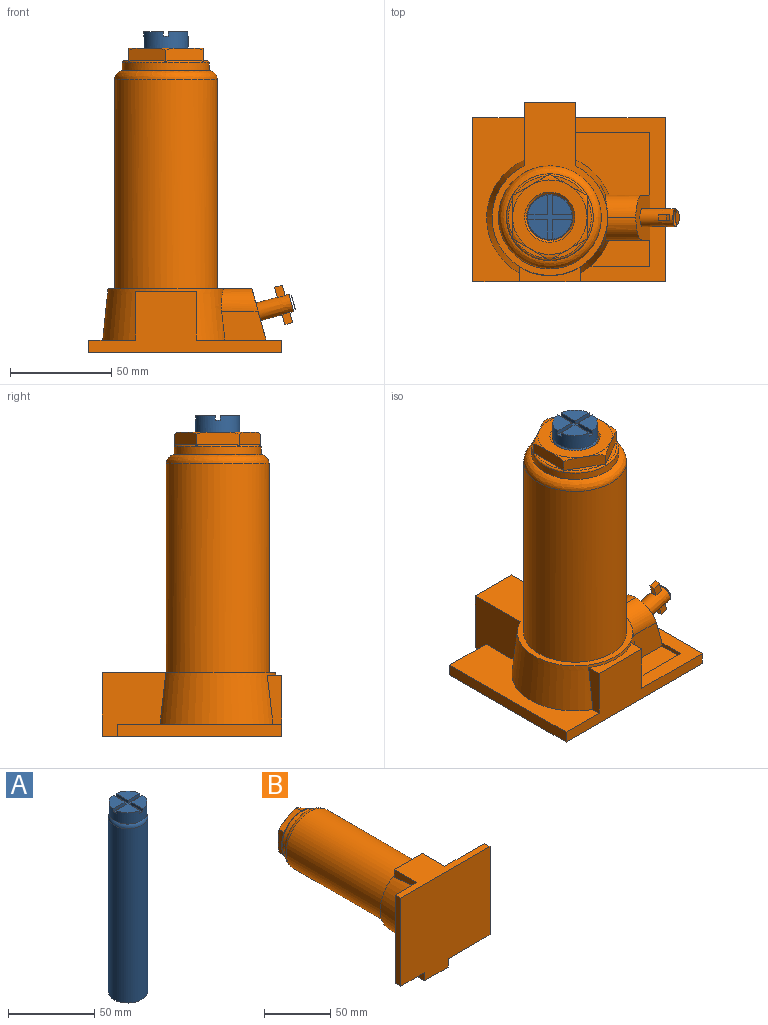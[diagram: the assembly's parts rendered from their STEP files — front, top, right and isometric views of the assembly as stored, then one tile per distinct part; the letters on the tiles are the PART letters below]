
ASSEMBLY  parts=2 mates=1
PART A: 18 faces, bbox 24.7x24.7x135 mm
  f0: plane 9.76x9.76mm, normal (0,0,1), area 70.6mm2, adj f2,f8,f16
  f1: plane 9.76x9.76mm, normal (0,0,1), area 70.6mm2, adj f3,f8,f15
  f2: plane 9.76x2.11mm, normal (0,1,0), area 20.6mm2, adj f0,f8,f11,f16
  f3: plane 9.76x2.11mm, normal (0,-1,0), area 20.6mm2, adj f1,f8,f11,f15
  f4: plane 9.76x9.76mm, normal (0,0,1), area 70.6mm2, adj f8,f12,f17
  f5: cylinder r=11.43mm len=124mm, axis (0,0,-1), area 8905.3mm2, adj f6,f7
  f6: plane 22.86x22.86mm, normal (0,0,-1), area 410.4mm2, adj f5
  f7: torus R=8.43mm, axis (0,0,1), area 306.2mm2, adj f5,f10
  f8: cylinder r=11mm len=22mm, axis (0,0,-1), area 533mm2, adj f0,f1,f2,f3,f4,f9,f10,f11
  f9: plane 9.76x9.76mm, normal (0,0,1), area 70.6mm2, adj f8,f13,f14
  f10: plane 22x22mm, normal (0,0,-1), area 156.9mm2, adj f7,f8
  f11: plane 22x22mm, normal (0,0,1), area 97.7mm2, adj f2,f3,f8,f12,f13,f14,f15,f16
  f12: plane 9.76x2.11mm, normal (0,1,0), area 20.6mm2, adj f4,f8,f11,f17
  f13: plane 9.76x2.11mm, normal (0,-1,0), area 20.6mm2, adj f8,f9,f11,f14
  f14: plane 9.76x2.11mm, normal (-1,0,0), area 20.6mm2, adj f8,f9,f11,f13
  f15: plane 9.76x2.11mm, normal (1,0,0), area 20.6mm2, adj f1,f3,f8,f11
  f16: plane 9.76x2.11mm, normal (1,0,0), area 20.6mm2, adj f0,f2,f8,f11
  f17: plane 9.76x2.11mm, normal (-1,0,0), area 20.6mm2, adj f4,f8,f11,f12
PART B: 70 faces, bbox 117.3x152.5x90.8 mm
  f0: plane 3.86x2.76mm, normal (0.27,-0.96,0), area 11mm2, adj f3,f4,f5,f6
  f1: plane 3.86x2.76mm, normal (-0.27,0.96,0), area 11mm2, adj f7,f8,f9,f10
  f2: plane 7x6.75mm, normal (0.96,0.27,0), area 38.5mm2, adj f11
  f3: plane 5.14x2.76mm, normal (0.96,0.27,0), area 14.3mm2, adj f0,f4,f6,f12
  f4: plane 6.2x5.27mm, normal (0,0,1), area 21.3mm2, adj f0,f3,f5,f12
  f5: plane 5.14x2.76mm, normal (-0.96,-0.27,0), area 14.3mm2, adj f0,f4,f6,f12
  f6: plane 6.2x5.27mm, normal (0,0,-1), area 21.3mm2, adj f0,f3,f5,f12
  f7: plane 5.14x2.76mm, normal (0.96,0.27,0), area 14.3mm2, adj f1,f8,f10,f12
  f8: plane 6.2x5.27mm, normal (0,0,-1), area 21.3mm2, adj f1,f7,f9,f12
  f9: plane 5.14x2.76mm, normal (-0.96,-0.27,0), area 14.3mm2, adj f1,f8,f10,f12
  f10: plane 6.2x5.27mm, normal (0,0,1), area 21.3mm2, adj f1,f7,f9,f12
  f11: revolved ~9x8.68mm, area 71.1mm2, adj f2,f12
  f12: revolved ~18.78x13.19mm, area 458.3mm2, adj f3,f4,f5,f6,f7,f8,f9,f10
  f13: plane 81.28x6mm, normal (1,0,0), area 487.7mm2, adj f17,f24,f25,f30
  f14: plane 29.68x2mm, normal (0,0,-1), area 59.4mm2, adj f18,f19,f29,f30
  f15: plane 30.73x2mm, normal (-1,0,0), area 61.5mm2, adj f22,f23,f27,f30
  f16: plane 81.28x6mm, normal (-1,0,0), area 487.7mm2, adj f17,f21,f25,f34
  f17: plane 95.25x29.91mm, normal (0,0,1), area 1288.7mm2, adj f13,f16,f25,f30,f31,f32,f33,f34
  f18: plane 12.95x2mm, normal (-1,0,0), area 25.9mm2, adj f14,f19,f30,f36
  f19: plane 29.68x12.96mm, normal (0,1,0), area 313mm2, adj f14,f18,f29,f36
  f20: plane 26.7x23.65mm, normal (0.96,0.27,0), area 469.7mm2, adj f12,f27,f28,f30,f35,f36
  f21: plane 25.4x6mm, normal (0,0,-1), area 152.4mm2, adj f16,f25,f34,f37
  f22: plane 36.83x30.74mm, normal (0,1,0), area 950.4mm2, adj f15,f23,f26,f27,f39
  f23: plane 36.83x2mm, normal (0,0,1), area 73.7mm2, adj f15,f22,f30,f39
  f24: plane 44.45x6mm, normal (0,0,-1), area 266.7mm2, adj f13,f25,f30,f39
  f25: plane 95.25x88.9mm, normal (0,-1,0), area 7935.5mm2, adj f13,f16,f17,f21,f24,f37,f38,f39
  f26: revolved ~17.37x16.48mm, area 49.1mm2, adj f22,f27,f39,f40
  f27: plane 22.16x16.43mm, normal (0,0,-1), area 313.8mm2, adj f15,f20,f22,f26,f28,f40
  f28: revolved ~18.05x11.18mm, area 281mm2, adj f20,f27,f35,f40
  f29: revolved ~12.95x9.33mm, area 32.3mm2, adj f14,f19,f36,f41
  f30: plane 81.28x44.45mm, normal (0,1,0), area 1154.6mm2, adj f13,f14,f15,f17,f18,f20,f23,f24
  f31: plane 24.58x7.92mm, normal (1,0,0), area 138.3mm2, adj f17,f30,f32,f41
  f32: plane 30x7.25mm, normal (0,1,0), area 131.5mm2, adj f17,f31,f33,f41
  f33: plane 24.58x7.92mm, normal (-1,0,0), area 138.3mm2, adj f17,f32,f34,f41
  f34: plane 81.28x25.4mm, normal (0,1,0), area 1293.6mm2, adj f16,f17,f21,f33,f37,f41
  f35: revolved ~18.05x11.18mm, area 281mm2, adj f20,f28,f36,f41
  f36: plane 22.16x16.43mm, normal (0,0,1), area 313.8mm2, adj f18,f19,f20,f29,f35,f41
  f37: plane 32.25x32.1mm, normal (-1,0,0), area 809.6mm2, adj f21,f25,f34,f38,f41,f43
  f38: plane 31.4x25.4mm, normal (0,0,-1), area 797.6mm2, adj f25,f37,f39,f43
  f39: plane 32.25x32.1mm, normal (1,0,0), area 836.3mm2, adj f22,f23,f24,f25,f26,f30,f38,f40
  f40: revolved ~28.55x25.4mm, area 600.8mm2, adj f26,f27,f28,f39,f43
  f41: revolved ~62.44x59.77mm, area 2243.3mm2, adj f29,f30,f31,f32,f33,f34,f35,f36
  f42: plane 22.86x22.86mm, normal (0,1,0), area 410.5mm2, adj f44
  f43: plane 85.75x57.17mm, normal (0,1,0), area 1289mm2, adj f37,f38,f39,f40,f41,f45
  f44: revolved ~118.08x22.86mm, area 8479.8mm2, adj f42,f46
  f45: revolved ~103.45x50.8mm, area 16509.9mm2, adj f43,f47
  f46: revolved ~24.86x24.86mm, area 106mm2, adj f44,f48
  f47: bspline ~102.74x51.37mm, area 1055.5mm2, adj f45,f49
  f48: plane 36.89x36.89mm, normal (0,1,0), area 579.6mm2, adj f46,f50,f51,f52,f53,f54,f55
  f49: plane 43.02x43.02mm, normal (0,-1,0), area 87.7mm2, adj f47,f56
  f50: bspline ~18.89x12.74mm, area 32.1mm2, adj f48,f58,f60
  f51: bspline ~18.89x12.74mm, area 32.1mm2, adj f48,f60,f62
  f52: bspline ~21.82x7.15mm, area 32.1mm2, adj f48,f62,f64
  f53: bspline ~18.89x12.74mm, area 32.1mm2, adj f48,f64,f66
  f54: bspline ~18.89x12.74mm, area 32.1mm2, adj f48,f66,f67
  f55: bspline ~21.82x7.15mm, area 32.1mm2, adj f48,f58,f67
  f56: revolved ~42.93x42.93mm, area 1018.2mm2, adj f49,f68
  f57: plane 15.61x9.08mm, normal (0,1,0), area 24.6mm2, adj f58,f68
  f58: plane 20.33x12.55mm, normal (0.5,0,-0.87), area 131mm2, adj f50,f55,f57,f60,f67,f68
  f59: plane 17.89x2.09mm, normal (0,1,0), area 24.6mm2, adj f60,f68
  f60: plane 23.19x8.68mm, normal (1,0,0), area 131mm2, adj f50,f51,f58,f59,f62,f68
  f61: plane 15.61x9.08mm, normal (0,1,0), area 24.6mm2, adj f62,f68
  f62: plane 20.33x12.55mm, normal (0.5,0,0.87), area 131mm2, adj f51,f52,f60,f61,f64,f68
  f63: plane 15.61x9.08mm, normal (0,1,0), area 24.6mm2, adj f64,f68
  f64: plane 20.33x12.55mm, normal (-0.5,0,0.87), area 131mm2, adj f52,f53,f62,f63,f66,f68
  f65: plane 17.89x2.09mm, normal (0,1,0), area 24.6mm2, adj f66,f68
  f66: plane 23.19x8.68mm, normal (-1,0,0), area 131mm2, adj f53,f54,f64,f65,f67,f68
  f67: plane 20.33x12.55mm, normal (-0.5,0,-0.87), area 131mm2, adj f54,f55,f58,f66,f68,f69
  f68: bspline ~86.11x43.05mm, area 200.5mm2, adj f56,f57,f58,f59,f60,f61,f62,f63
  f69: plane 15.61x9.08mm, normal (0,1,0), area 24.6mm2, adj f67,f68
PLACE A rot(axis=(0,0,1),90deg) t=(-9.29,-9.97,23.48)mm
PLACE B rot(axis=(1,0,0),90deg) t=(-9.29,-9.97,31.4)mm
MATE cylindrical A.f5 <-> B.f48  axis (0,0,1) through (-9.29,-9.97,150.48)mm
